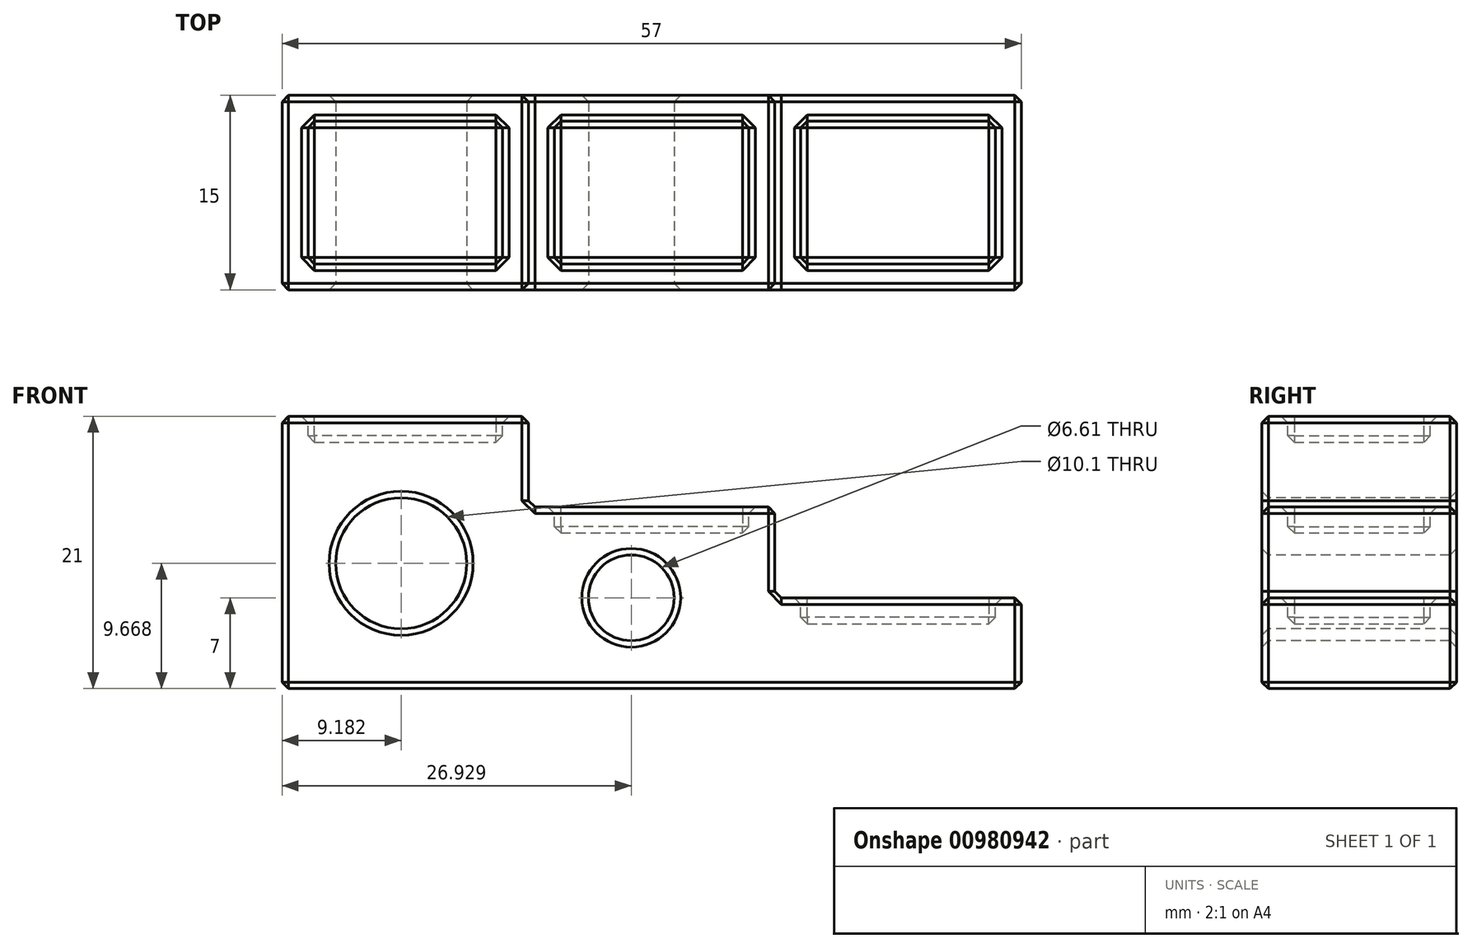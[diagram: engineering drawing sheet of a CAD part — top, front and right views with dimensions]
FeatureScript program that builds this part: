
annotation { "Feature Type Name" : "Feature", "Feature Type Description" : "" }
export const myFeature = defineFeature(function(context is Context, id is Id, definition is map)
    precondition{}
    {
        {
            var Q0;
            Q0=qCreatedBy(makeId("Front.planeOp"),FACE);
            var sketch = newSketch(context, id + "F0", { "sketchPlane" : qUnion([Q0])});
            skLineSegment(sketch, "E0", {"start": v(0, 0) * mm, "end": v(57, 0) * mm});
            skLineSegment(sketch, "E1", {"start": v(57, 0) * mm, "end": v(57, 7) * mm});
            skLineSegment(sketch, "E2", {"start": v(57, 7) * mm, "end": v(38, 7) * mm});
            skLineSegment(sketch, "E3", {"start": v(38, 7) * mm, "end": v(38, 14) * mm});
            skLineSegment(sketch, "E4", {"start": v(38, 14) * mm, "end": v(19, 14) * mm});
            skLineSegment(sketch, "E5", {"start": v(19, 14) * mm, "end": v(19, 21) * mm});
            skLineSegment(sketch, "E6", {"start": v(19, 21) * mm, "end": v(0, 21) * mm});
            skLineSegment(sketch, "E7", {"start": v(0, 21) * mm, "end": v(0, 0) * mm});
            skSolve(sketch);
        }
        {
            var Q0;
            Q0 = qSketchRegion(id + "F0", true);
            extrude(context, id + "F1", {"entities" : qUnion([Q0]), "depth" : 15 * mm, "offsetDistance" : 25 * mm});
        }
        {
            var Q0;
            Q0=makeQuery(id+"F1.opExtrude","SWEPT_FACE",FACE,{"disambiguationData":[OSD([sQuery(id+"F0.wireOp",EDGE,"E6")])]});
            var sketch = newSketch(context, id + "F2", { "sketchPlane" : qUnion([Q0])});
            skLineSegment(sketch, "E8.bottom", {"start": v(2, -13) * mm, "end": v(17, -13) * mm});
            skLineSegment(sketch, "E8.top", {"start": v(2, -2) * mm, "end": v(17, -2) * mm});
            skLineSegment(sketch, "E8.left", {"start": v(2, -13) * mm, "end": v(2, -2) * mm});
            skLineSegment(sketch, "E8.right", {"start": v(17, -13) * mm, "end": v(17, -2) * mm});
            skSolve(sketch);
        }
        {
            var Q0;
            Q0 = qSketchRegion(id + "F2", true);
            extrude(context, id + "F3", {"entities" : qUnion([Q0]), "operationType" : NewBodyOperationType.REMOVE, "oppositeDirection" : true, "depth" : 2 * mm, "offsetDistance" : 25 * mm});
        }
        {
            var Q0;
            Q0=makeQuery(id+"F1.opExtrude","SWEPT_FACE",FACE,{"disambiguationData":[OSD([sQuery(id+"F0.wireOp",EDGE,"E4")])]});
            var sketch = newSketch(context, id + "F4", { "sketchPlane" : qUnion([Q0])});
            skLineSegment(sketch, "E9.bottom", {"start": v(21, -13) * mm, "end": v(36, -13) * mm});
            skLineSegment(sketch, "E9.top", {"start": v(21, -2) * mm, "end": v(36, -2) * mm});
            skLineSegment(sketch, "E9.left", {"start": v(21, -13) * mm, "end": v(21, -2) * mm});
            skLineSegment(sketch, "E9.right", {"start": v(36, -13) * mm, "end": v(36, -2) * mm});
            skSolve(sketch);
        }
        {
            var Q0;
            Q0 = qSketchRegion(id + "F4", true);
            extrude(context, id + "F5", {"entities" : qUnion([Q0]), "operationType" : NewBodyOperationType.REMOVE, "oppositeDirection" : true, "depth" : 2 * mm, "offsetDistance" : 25 * mm});
        }
        {
            var Q0;
            Q0=makeQuery(id+"F1.opExtrude","SWEPT_FACE",FACE,{"disambiguationData":[OSD([sQuery(id+"F0.wireOp",EDGE,"E2")])]});
            var sketch = newSketch(context, id + "F6", { "sketchPlane" : qUnion([Q0])});
            skLineSegment(sketch, "E10.bottom", {"start": v(40, -13) * mm, "end": v(55, -13) * mm});
            skLineSegment(sketch, "E10.top", {"start": v(40, -2) * mm, "end": v(55, -2) * mm});
            skLineSegment(sketch, "E10.left", {"start": v(40, -13) * mm, "end": v(40, -2) * mm});
            skLineSegment(sketch, "E10.right", {"start": v(55, -13) * mm, "end": v(55, -2) * mm});
            skSolve(sketch);
        }
        {
            var Q0;
            Q0 = qSketchRegion(id + "F6", true);
            extrude(context, id + "F7", {"entities" : qUnion([Q0]), "operationType" : NewBodyOperationType.REMOVE, "oppositeDirection" : true, "depth" : 2 * mm, "offsetDistance" : 25 * mm});
        }
        {
            var Q0;
            Q0=makeQuery(id+"F1.opExtrude","CAP_FACE",FACE,{"disambiguationData":[OSD([sQuery(id+"F0.wireOp",EDGE,"E0"),sQuery(id+"F0.wireOp",EDGE,"E1"),sQuery(id+"F0.wireOp",EDGE,"E2"),sQuery(id+"F0.wireOp",EDGE,"E3"),sQuery(id+"F0.wireOp",EDGE,"E4"),sQuery(id+"F0.wireOp",EDGE,"E5"),sQuery(id+"F0.wireOp",EDGE,"E6"),sQuery(id+"F0.wireOp",EDGE,"E7")])],"isStart":false});
            var sketch = newSketch(context, id + "F8", { "sketchPlane" : qUnion([Q0])});
            skCircle(sketch, "E11", {"center": v(9.18, 9.67) * mm, "radius": 5.05 * mm});
            skCircle(sketch, "E12", {"center": v(26.93, 7) * mm, "radius": 3.3 * mm});
            skSolve(sketch);
        }
        {
            var Q0;
            Q0 = qSketchRegion(id + "F8", true);
            extrude(context, id + "F9", {"entities" : qUnion([Q0]), "operationType" : NewBodyOperationType.REMOVE, "oppositeDirection" : true, "depth" : 25 * mm, "offsetDistance" : 25 * mm});
        }
        {
            var Q0;
            Q0=makeQuery(id+"F1.opExtrude","CAP_EDGE",EDGE,{"disambiguationData":[OSD([sQuery(id+"F0.wireOp",EDGE,"E4")])],"isStart":true});
            var Q1;
            Q1=makeQuery(id+"F1.opExtrude","CAP_EDGE",EDGE,{"disambiguationData":[OSD([sQuery(id+"F0.wireOp",EDGE,"E4")])],"isStart":false});
            var Q2;
            Q2=makeQuery(id+"F1.opExtrude","CAP_EDGE",EDGE,{"disambiguationData":[OSD([sQuery(id+"F0.wireOp",EDGE,"E2")])],"isStart":true});
            var Q3;
            Q3=makeQuery(id+"F1.opExtrude","SWEPT_FACE",FACE,{"disambiguationData":[OSD([sQuery(id+"F0.wireOp",EDGE,"E7")])]});
            var Q4;
            Q4=makeQuery(id+"F1.opExtrude","CAP_EDGE",EDGE,{"disambiguationData":[OSD([sQuery(id+"F0.wireOp",EDGE,"E0")])],"isStart":false});
            var Q5;
            Q5=makeQuery(id+"F1.opExtrude","SWEPT_FACE",FACE,{"disambiguationData":[OSD([sQuery(id+"F0.wireOp",EDGE,"E5")])]});
            var Q6;
            Q6=makeQuery(id+"F1.opExtrude","SWEPT_EDGE",EDGE,{"disambiguationData":[OSD([sQuery(id+"F0.wireOp",EDGE,"E6"),sQuery(id+"F0.wireOp",EDGE,"E7")])]});
            var Q7;
            Q7=makeQuery(id+"F1.opExtrude","SWEPT_EDGE",EDGE,{"disambiguationData":[OSD([sQuery(id+"F0.wireOp",EDGE,"E5"),sQuery(id+"F0.wireOp",EDGE,"E6")])]});
            var Q8;
            Q8=makeQuery(id+"F1.opExtrude","SWEPT_FACE",FACE,{"disambiguationData":[OSD([sQuery(id+"F0.wireOp",EDGE,"E3")])]});
            var Q9;
            Q9=makeQuery(id+"F1.opExtrude","SWEPT_EDGE",EDGE,{"disambiguationData":[OSD([sQuery(id+"F0.wireOp",EDGE,"E4"),sQuery(id+"F0.wireOp",EDGE,"E5")])]});
            var Q10;
            Q10=makeQuery(id+"F1.opExtrude","SWEPT_EDGE",EDGE,{"disambiguationData":[OSD([sQuery(id+"F0.wireOp",EDGE,"E3"),sQuery(id+"F0.wireOp",EDGE,"E4")])]});
            var Q11;
            Q11=makeQuery(id+"F1.opExtrude","SWEPT_FACE",FACE,{"disambiguationData":[OSD([sQuery(id+"F0.wireOp",EDGE,"E1")])]});
            var Q12;
            Q12=makeQuery(id+"F1.opExtrude","SWEPT_EDGE",EDGE,{"disambiguationData":[OSD([sQuery(id+"F0.wireOp",EDGE,"E2"),sQuery(id+"F0.wireOp",EDGE,"E3")])]});
            var Q13;
            Q13=makeQuery(id+"F9.boolean.opBoolean","COPY",FACE,{"derivedFrom":makeQuery(id+"F9.opExtrude","SWEPT_FACE",FACE,{"disambiguationData":[OSD([sQuery(id+"F8.wireOp",EDGE,"E11")])]})});
            var Q14;
            Q14=makeQuery(id+"F1.opExtrude","SWEPT_EDGE",EDGE,{"disambiguationData":[OSD([sQuery(id+"F0.wireOp",EDGE,"E1"),sQuery(id+"F0.wireOp",EDGE,"E2")])]});
            var Q15;
            Q15=makeQuery(id+"F1.opExtrude","SWEPT_EDGE",EDGE,{"disambiguationData":[OSD([sQuery(id+"F0.wireOp",EDGE,"E0"),sQuery(id+"F0.wireOp",EDGE,"E1")])]});
            var Q16;
            Q16=makeQuery(id+"F1.opExtrude","SWEPT_FACE",FACE,{"disambiguationData":[OSD([sQuery(id+"F0.wireOp",EDGE,"E0")])]});
            var Q17;
            Q17=makeQuery(id+"F1.opExtrude","CAP_EDGE",EDGE,{"disambiguationData":[OSD([sQuery(id+"F0.wireOp",EDGE,"E2")])],"isStart":false});
            var Q18;
            Q18=makeQuery(id+"F1.opExtrude","CAP_EDGE",EDGE,{"disambiguationData":[OSD([sQuery(id+"F0.wireOp",EDGE,"E6")])],"isStart":true});
            var Q19;
            Q19=makeQuery(id+"F1.opExtrude","CAP_EDGE",EDGE,{"disambiguationData":[OSD([sQuery(id+"F0.wireOp",EDGE,"E6")])],"isStart":false});
            var Q20;
            Q20=makeQuery(id+"F3.boolean.opBoolean","COPY",FACE,{"derivedFrom":makeQuery(id+"F3.opExtrude","SWEPT_FACE",FACE,{"disambiguationData":[OSD([sQuery(id+"F2.wireOp",EDGE,"E8.bottom")])]})});
            var Q21;
            Q21=makeQuery(id+"F3.boolean.opBoolean","COPY",FACE,{"derivedFrom":makeQuery(id+"F3.opExtrude","CAP_FACE",FACE,{"disambiguationData":[OSD([sQuery(id+"F2.wireOp",EDGE,"E8.bottom"),sQuery(id+"F2.wireOp",EDGE,"E8.top"),sQuery(id+"F2.wireOp",EDGE,"E8.left"),sQuery(id+"F2.wireOp",EDGE,"E8.right")])],"isStart":false})});
            var Q22;
            Q22=makeQuery(id+"F3.boolean.opBoolean","COPY",FACE,{"derivedFrom":makeQuery(id+"F3.opExtrude","SWEPT_FACE",FACE,{"disambiguationData":[OSD([sQuery(id+"F2.wireOp",EDGE,"E8.top")])]})});
            var Q23;
            Q23=makeQuery(id+"F3.boolean.opBoolean","COPY",FACE,{"derivedFrom":makeQuery(id+"F3.opExtrude","SWEPT_FACE",FACE,{"disambiguationData":[OSD([sQuery(id+"F2.wireOp",EDGE,"E8.left")])]})});
            var Q24;
            Q24=makeQuery(id+"F3.boolean.opBoolean","COPY",EDGE,{"derivedFrom":makeQuery(id+"F3.opExtrude","CAP_EDGE",EDGE,{"disambiguationData":[OSD([sQuery(id+"F2.wireOp",EDGE,"E8.bottom")])],"isStart":true})});
            var Q25;
            Q25=makeQuery(id+"F3.boolean.opBoolean","COPY",FACE,{"derivedFrom":makeQuery(id+"F3.opExtrude","SWEPT_FACE",FACE,{"disambiguationData":[OSD([sQuery(id+"F2.wireOp",EDGE,"E8.right")])]})});
            var Q26;
            Q26=makeQuery(id+"F1.opExtrude","SWEPT_FACE",FACE,{"disambiguationData":[OSD([sQuery(id+"F0.wireOp",EDGE,"E6")])]});
            var Q27;
            Q27=makeQuery(id+"F3.boolean.opBoolean","COPY",EDGE,{"derivedFrom":makeQuery(id+"F3.opExtrude","CAP_EDGE",EDGE,{"disambiguationData":[OSD([sQuery(id+"F2.wireOp",EDGE,"E8.top")])],"isStart":true})});
            var Q28;
            Q28=makeQuery(id+"F3.boolean.opBoolean","COPY",EDGE,{"derivedFrom":makeQuery(id+"F3.opExtrude","CAP_EDGE",EDGE,{"disambiguationData":[OSD([sQuery(id+"F2.wireOp",EDGE,"E8.top")])],"isStart":false})});
            var Q29;
            Q29=makeQuery(id+"F3.boolean.opBoolean","COPY",EDGE,{"derivedFrom":makeQuery(id+"F3.opExtrude","CAP_EDGE",EDGE,{"disambiguationData":[OSD([sQuery(id+"F2.wireOp",EDGE,"E8.left")])],"isStart":false})});
            var Q30;
            Q30=makeQuery(id+"F5.boolean.opBoolean","COPY",FACE,{"derivedFrom":makeQuery(id+"F5.opExtrude","SWEPT_FACE",FACE,{"disambiguationData":[OSD([sQuery(id+"F4.wireOp",EDGE,"E9.bottom")])]})});
            var Q31;
            Q31=makeQuery(id+"F5.boolean.opBoolean","COPY",FACE,{"derivedFrom":makeQuery(id+"F5.opExtrude","CAP_FACE",FACE,{"disambiguationData":[OSD([sQuery(id+"F4.wireOp",EDGE,"E9.bottom"),sQuery(id+"F4.wireOp",EDGE,"E9.top"),sQuery(id+"F4.wireOp",EDGE,"E9.left"),sQuery(id+"F4.wireOp",EDGE,"E9.right")])],"isStart":false})});
            var Q32;
            Q32=makeQuery(id+"F5.boolean.opBoolean","COPY",FACE,{"derivedFrom":makeQuery(id+"F5.opExtrude","SWEPT_FACE",FACE,{"disambiguationData":[OSD([sQuery(id+"F4.wireOp",EDGE,"E9.top")])]})});
            var Q33;
            Q33=makeQuery(id+"F5.boolean.opBoolean","COPY",FACE,{"derivedFrom":makeQuery(id+"F5.opExtrude","SWEPT_FACE",FACE,{"disambiguationData":[OSD([sQuery(id+"F4.wireOp",EDGE,"E9.left")])]})});
            var Q34;
            Q34=makeQuery(id+"F5.boolean.opBoolean","COPY",EDGE,{"derivedFrom":makeQuery(id+"F5.opExtrude","CAP_EDGE",EDGE,{"disambiguationData":[OSD([sQuery(id+"F4.wireOp",EDGE,"E9.bottom")])],"isStart":true})});
            var Q35;
            Q35=makeQuery(id+"F5.boolean.opBoolean","COPY",FACE,{"derivedFrom":makeQuery(id+"F5.opExtrude","SWEPT_FACE",FACE,{"disambiguationData":[OSD([sQuery(id+"F4.wireOp",EDGE,"E9.right")])]})});
            var Q36;
            Q36=makeQuery(id+"F1.opExtrude","SWEPT_FACE",FACE,{"disambiguationData":[OSD([sQuery(id+"F0.wireOp",EDGE,"E4")])]});
            var Q37;
            Q37=makeQuery(id+"F5.boolean.opBoolean","COPY",EDGE,{"derivedFrom":makeQuery(id+"F5.opExtrude","CAP_EDGE",EDGE,{"disambiguationData":[OSD([sQuery(id+"F4.wireOp",EDGE,"E9.top")])],"isStart":false})});
            var Q38;
            Q38=makeQuery(id+"F7.boolean.opBoolean","COPY",FACE,{"derivedFrom":makeQuery(id+"F7.opExtrude","SWEPT_FACE",FACE,{"disambiguationData":[OSD([sQuery(id+"F6.wireOp",EDGE,"E10.bottom")])]})});
            var Q39;
            Q39=makeQuery(id+"F7.boolean.opBoolean","COPY",FACE,{"derivedFrom":makeQuery(id+"F7.opExtrude","CAP_FACE",FACE,{"disambiguationData":[OSD([sQuery(id+"F6.wireOp",EDGE,"E10.bottom"),sQuery(id+"F6.wireOp",EDGE,"E10.top"),sQuery(id+"F6.wireOp",EDGE,"E10.left"),sQuery(id+"F6.wireOp",EDGE,"E10.right")])],"isStart":false})});
            var Q40;
            Q40=makeQuery(id+"F7.boolean.opBoolean","COPY",FACE,{"derivedFrom":makeQuery(id+"F7.opExtrude","SWEPT_FACE",FACE,{"disambiguationData":[OSD([sQuery(id+"F6.wireOp",EDGE,"E10.top")])]})});
            var Q41;
            Q41=makeQuery(id+"F7.boolean.opBoolean","COPY",FACE,{"derivedFrom":makeQuery(id+"F7.opExtrude","SWEPT_FACE",FACE,{"disambiguationData":[OSD([sQuery(id+"F6.wireOp",EDGE,"E10.left")])]})});
            var Q42;
            Q42=makeQuery(id+"F7.boolean.opBoolean","COPY",FACE,{"derivedFrom":makeQuery(id+"F7.opExtrude","SWEPT_FACE",FACE,{"disambiguationData":[OSD([sQuery(id+"F6.wireOp",EDGE,"E10.right")])]})});
            var Q43;
            Q43=makeQuery(id+"F1.opExtrude","SWEPT_FACE",FACE,{"disambiguationData":[OSD([sQuery(id+"F0.wireOp",EDGE,"E2")])]});
            var Q44;
            Q44=makeQuery(id+"F7.boolean.opBoolean","COPY",EDGE,{"derivedFrom":makeQuery(id+"F7.opExtrude","CAP_EDGE",EDGE,{"disambiguationData":[OSD([sQuery(id+"F6.wireOp",EDGE,"E10.top")])],"isStart":true})});
            var Q45;
            Q45=makeQuery(id+"F7.boolean.opBoolean","COPY",EDGE,{"derivedFrom":makeQuery(id+"F7.opExtrude","CAP_EDGE",EDGE,{"disambiguationData":[OSD([sQuery(id+"F6.wireOp",EDGE,"E10.top")])],"isStart":false})});
            var Q46;
            Q46=makeQuery(id+"F1.opExtrude","CAP_FACE",FACE,{"disambiguationData":[OSD([sQuery(id+"F0.wireOp",EDGE,"E0"),sQuery(id+"F0.wireOp",EDGE,"E1"),sQuery(id+"F0.wireOp",EDGE,"E2"),sQuery(id+"F0.wireOp",EDGE,"E3"),sQuery(id+"F0.wireOp",EDGE,"E4"),sQuery(id+"F0.wireOp",EDGE,"E5"),sQuery(id+"F0.wireOp",EDGE,"E6"),sQuery(id+"F0.wireOp",EDGE,"E7")])],"isStart":false});
            var Q47;
            Q47=makeQuery(id+"F9.boolean.opBoolean","COPY",EDGE,{"derivedFrom":makeQuery(id+"F9.opExtrude","CAP_EDGE",EDGE,{"disambiguationData":[OSD([sQuery(id+"F8.wireOp",EDGE,"E12")])],"isStart":true})});
            var Q48;
            Q48=makeQuery(id+"F9.boolean.opBoolean","COPY",EDGE,{"derivedFrom":makeQuery(id+"F9.opExtrude","CAP_EDGE",EDGE,{"disambiguationData":[OSD([sQuery(id+"F8.wireOp",EDGE,"E11")])],"isStart":true})});
            var Q49;
            Q49=makeQuery(id+"F9.boolean.opBoolean","COPY",FACE,{"derivedFrom":makeQuery(id+"F9.opExtrude","SWEPT_FACE",FACE,{"disambiguationData":[OSD([sQuery(id+"F8.wireOp",EDGE,"E12")])]})});
            var Q50;
            Q50=makeQuery(id+"F1.opExtrude","CAP_EDGE",EDGE,{"disambiguationData":[OSD([sQuery(id+"F0.wireOp",EDGE,"E7")])],"isStart":false});
            var Q51;
            Q51=makeQuery(id+"F1.opExtrude","CAP_EDGE",EDGE,{"disambiguationData":[OSD([sQuery(id+"F0.wireOp",EDGE,"E1")])],"isStart":false});
            var Q52;
            Q52=makeQuery(id+"F1.opExtrude","CAP_EDGE",EDGE,{"disambiguationData":[OSD([sQuery(id+"F0.wireOp",EDGE,"E1")])],"isStart":true});
            var Q53;
            Q53=makeQuery(id+"F1.opExtrude","CAP_EDGE",EDGE,{"disambiguationData":[OSD([sQuery(id+"F0.wireOp",EDGE,"E0")])],"isStart":true});
            var Q54;
            Q54=makeQuery(id+"F1.opExtrude","SWEPT_EDGE",EDGE,{"disambiguationData":[OSD([sQuery(id+"F0.wireOp",EDGE,"E0"),sQuery(id+"F0.wireOp",EDGE,"E7")])]});
            var Q55;
            Q55=makeQuery(id+"F1.opExtrude","CAP_EDGE",EDGE,{"disambiguationData":[OSD([sQuery(id+"F0.wireOp",EDGE,"E3")])],"isStart":true});
            var Q56;
            Q56=makeQuery(id+"F1.opExtrude","CAP_EDGE",EDGE,{"disambiguationData":[OSD([sQuery(id+"F0.wireOp",EDGE,"E5")])],"isStart":true});
            var Q57;
            Q57=makeQuery(id+"F1.opExtrude","CAP_EDGE",EDGE,{"disambiguationData":[OSD([sQuery(id+"F0.wireOp",EDGE,"E5")])],"isStart":false});
            var Q58;
            Q58=makeQuery(id+"F1.opExtrude","CAP_EDGE",EDGE,{"disambiguationData":[OSD([sQuery(id+"F0.wireOp",EDGE,"E3")])],"isStart":false});
            var Q59;
            Q59=makeQuery(id+"F1.opExtrude","CAP_EDGE",EDGE,{"disambiguationData":[OSD([sQuery(id+"F0.wireOp",EDGE,"E7")])],"isStart":true});
            var Q60;
            Q60=makeQuery(id+"F3.boolean.opBoolean","COPY",EDGE,{"derivedFrom":makeQuery(id+"F3.opExtrude","SWEPT_EDGE",EDGE,{"disambiguationData":[OSD([sQuery(id+"F2.wireOp",EDGE,"E8.bottom"),sQuery(id+"F2.wireOp",EDGE,"E8.left")])]})});
            var Q61;
            Q61=makeQuery(id+"F3.boolean.opBoolean","COPY",EDGE,{"derivedFrom":makeQuery(id+"F3.opExtrude","SWEPT_EDGE",EDGE,{"disambiguationData":[OSD([sQuery(id+"F2.wireOp",EDGE,"E8.bottom"),sQuery(id+"F2.wireOp",EDGE,"E8.right")])]})});
            var Q62;
            Q62=makeQuery(id+"F3.boolean.opBoolean","COPY",EDGE,{"derivedFrom":makeQuery(id+"F3.opExtrude","SWEPT_EDGE",EDGE,{"disambiguationData":[OSD([sQuery(id+"F2.wireOp",EDGE,"E8.top"),sQuery(id+"F2.wireOp",EDGE,"E8.left")])]})});
            var Q63;
            Q63=makeQuery(id+"F3.boolean.opBoolean","COPY",EDGE,{"derivedFrom":makeQuery(id+"F3.opExtrude","SWEPT_EDGE",EDGE,{"disambiguationData":[OSD([sQuery(id+"F2.wireOp",EDGE,"E8.top"),sQuery(id+"F2.wireOp",EDGE,"E8.right")])]})});
            var Q64;
            Q64=makeQuery(id+"F3.boolean.opBoolean","COPY",EDGE,{"derivedFrom":makeQuery(id+"F3.opExtrude","CAP_EDGE",EDGE,{"disambiguationData":[OSD([sQuery(id+"F2.wireOp",EDGE,"E8.bottom")])],"isStart":false})});
            var Q65;
            Q65=makeQuery(id+"F3.boolean.opBoolean","COPY",EDGE,{"derivedFrom":makeQuery(id+"F3.opExtrude","CAP_EDGE",EDGE,{"disambiguationData":[OSD([sQuery(id+"F2.wireOp",EDGE,"E8.left")])],"isStart":true})});
            var Q66;
            Q66=makeQuery(id+"F3.boolean.opBoolean","COPY",EDGE,{"derivedFrom":makeQuery(id+"F3.opExtrude","CAP_EDGE",EDGE,{"disambiguationData":[OSD([sQuery(id+"F2.wireOp",EDGE,"E8.right")])],"isStart":true})});
            var Q67;
            Q67=makeQuery(id+"F3.boolean.opBoolean","COPY",EDGE,{"derivedFrom":makeQuery(id+"F3.opExtrude","CAP_EDGE",EDGE,{"disambiguationData":[OSD([sQuery(id+"F2.wireOp",EDGE,"E8.right")])],"isStart":false})});
            var Q68;
            Q68=makeQuery(id+"F5.boolean.opBoolean","COPY",EDGE,{"derivedFrom":makeQuery(id+"F5.opExtrude","SWEPT_EDGE",EDGE,{"disambiguationData":[OSD([sQuery(id+"F4.wireOp",EDGE,"E9.bottom"),sQuery(id+"F4.wireOp",EDGE,"E9.left")])]})});
            var Q69;
            Q69=makeQuery(id+"F5.boolean.opBoolean","COPY",EDGE,{"derivedFrom":makeQuery(id+"F5.opExtrude","SWEPT_EDGE",EDGE,{"disambiguationData":[OSD([sQuery(id+"F4.wireOp",EDGE,"E9.top"),sQuery(id+"F4.wireOp",EDGE,"E9.left")])]})});
            var Q70;
            Q70=makeQuery(id+"F5.boolean.opBoolean","COPY",EDGE,{"derivedFrom":makeQuery(id+"F5.opExtrude","SWEPT_EDGE",EDGE,{"disambiguationData":[OSD([sQuery(id+"F4.wireOp",EDGE,"E9.top"),sQuery(id+"F4.wireOp",EDGE,"E9.right")])]})});
            var Q71;
            Q71=makeQuery(id+"F5.boolean.opBoolean","COPY",EDGE,{"derivedFrom":makeQuery(id+"F5.opExtrude","CAP_EDGE",EDGE,{"disambiguationData":[OSD([sQuery(id+"F4.wireOp",EDGE,"E9.bottom")])],"isStart":false})});
            var Q72;
            Q72=makeQuery(id+"F5.boolean.opBoolean","COPY",EDGE,{"derivedFrom":makeQuery(id+"F5.opExtrude","CAP_EDGE",EDGE,{"disambiguationData":[OSD([sQuery(id+"F4.wireOp",EDGE,"E9.top")])],"isStart":true})});
            var Q73;
            Q73=makeQuery(id+"F5.boolean.opBoolean","COPY",EDGE,{"derivedFrom":makeQuery(id+"F5.opExtrude","CAP_EDGE",EDGE,{"disambiguationData":[OSD([sQuery(id+"F4.wireOp",EDGE,"E9.left")])],"isStart":true})});
            var Q74;
            Q74=makeQuery(id+"F5.boolean.opBoolean","COPY",EDGE,{"derivedFrom":makeQuery(id+"F5.opExtrude","CAP_EDGE",EDGE,{"disambiguationData":[OSD([sQuery(id+"F4.wireOp",EDGE,"E9.left")])],"isStart":false})});
            var Q75;
            Q75=makeQuery(id+"F5.boolean.opBoolean","COPY",EDGE,{"derivedFrom":makeQuery(id+"F5.opExtrude","CAP_EDGE",EDGE,{"disambiguationData":[OSD([sQuery(id+"F4.wireOp",EDGE,"E9.right")])],"isStart":true})});
            var Q76;
            Q76=makeQuery(id+"F5.boolean.opBoolean","COPY",EDGE,{"derivedFrom":makeQuery(id+"F5.opExtrude","CAP_EDGE",EDGE,{"disambiguationData":[OSD([sQuery(id+"F4.wireOp",EDGE,"E9.right")])],"isStart":false})});
            var Q77;
            Q77=makeQuery(id+"F7.boolean.opBoolean","COPY",EDGE,{"derivedFrom":makeQuery(id+"F7.opExtrude","SWEPT_EDGE",EDGE,{"disambiguationData":[OSD([sQuery(id+"F6.wireOp",EDGE,"E10.bottom"),sQuery(id+"F6.wireOp",EDGE,"E10.left")])]})});
            var Q78;
            Q78=makeQuery(id+"F7.boolean.opBoolean","COPY",EDGE,{"derivedFrom":makeQuery(id+"F7.opExtrude","SWEPT_EDGE",EDGE,{"disambiguationData":[OSD([sQuery(id+"F6.wireOp",EDGE,"E10.bottom"),sQuery(id+"F6.wireOp",EDGE,"E10.right")])]})});
            var Q79;
            Q79=makeQuery(id+"F7.boolean.opBoolean","COPY",EDGE,{"derivedFrom":makeQuery(id+"F7.opExtrude","SWEPT_EDGE",EDGE,{"disambiguationData":[OSD([sQuery(id+"F6.wireOp",EDGE,"E10.top"),sQuery(id+"F6.wireOp",EDGE,"E10.left")])]})});
            var Q80;
            Q80=makeQuery(id+"F7.boolean.opBoolean","COPY",EDGE,{"derivedFrom":makeQuery(id+"F7.opExtrude","SWEPT_EDGE",EDGE,{"disambiguationData":[OSD([sQuery(id+"F6.wireOp",EDGE,"E10.top"),sQuery(id+"F6.wireOp",EDGE,"E10.right")])]})});
            var Q81;
            Q81=makeQuery(id+"F7.boolean.opBoolean","COPY",EDGE,{"derivedFrom":makeQuery(id+"F7.opExtrude","CAP_EDGE",EDGE,{"disambiguationData":[OSD([sQuery(id+"F6.wireOp",EDGE,"E10.bottom")])],"isStart":true})});
            var Q82;
            Q82=makeQuery(id+"F7.boolean.opBoolean","COPY",EDGE,{"derivedFrom":makeQuery(id+"F7.opExtrude","CAP_EDGE",EDGE,{"disambiguationData":[OSD([sQuery(id+"F6.wireOp",EDGE,"E10.bottom")])],"isStart":false})});
            var Q83;
            Q83=makeQuery(id+"F7.boolean.opBoolean","COPY",EDGE,{"derivedFrom":makeQuery(id+"F7.opExtrude","CAP_EDGE",EDGE,{"disambiguationData":[OSD([sQuery(id+"F6.wireOp",EDGE,"E10.left")])],"isStart":true})});
            var Q84;
            Q84=makeQuery(id+"F7.boolean.opBoolean","COPY",EDGE,{"derivedFrom":makeQuery(id+"F7.opExtrude","CAP_EDGE",EDGE,{"disambiguationData":[OSD([sQuery(id+"F6.wireOp",EDGE,"E10.left")])],"isStart":false})});
            var Q85;
            Q85=makeQuery(id+"F7.boolean.opBoolean","COPY",EDGE,{"derivedFrom":makeQuery(id+"F7.opExtrude","CAP_EDGE",EDGE,{"disambiguationData":[OSD([sQuery(id+"F6.wireOp",EDGE,"E10.right")])],"isStart":true})});
            var Q86;
            Q86=makeQuery(id+"F7.boolean.opBoolean","COPY",EDGE,{"derivedFrom":makeQuery(id+"F7.opExtrude","CAP_EDGE",EDGE,{"disambiguationData":[OSD([sQuery(id+"F6.wireOp",EDGE,"E10.right")])],"isStart":false})});
            var Q87;
            Q87=makeQuery(id+"F9.boolean.opBoolean","INTERSECT",EDGE,{"derivedFrom":[makeQuery(id+"F1.opExtrude","CAP_FACE",FACE,{"disambiguationData":[OSD([sQuery(id+"F0.wireOp",EDGE,"E0"),sQuery(id+"F0.wireOp",EDGE,"E1"),sQuery(id+"F0.wireOp",EDGE,"E2"),sQuery(id+"F0.wireOp",EDGE,"E3"),sQuery(id+"F0.wireOp",EDGE,"E4"),sQuery(id+"F0.wireOp",EDGE,"E5"),sQuery(id+"F0.wireOp",EDGE,"E6"),sQuery(id+"F0.wireOp",EDGE,"E7")])],"isStart":true}),makeQuery(id+"F9.opExtrude","SWEPT_FACE",FACE,{"disambiguationData":[OSD([sQuery(id+"F8.wireOp",EDGE,"E12")])]})]});
            var Q88;
            Q88=makeQuery(id+"F1.opExtrude","CAP_FACE",FACE,{"disambiguationData":[OSD([sQuery(id+"F0.wireOp",EDGE,"E0"),sQuery(id+"F0.wireOp",EDGE,"E1"),sQuery(id+"F0.wireOp",EDGE,"E2"),sQuery(id+"F0.wireOp",EDGE,"E3"),sQuery(id+"F0.wireOp",EDGE,"E4"),sQuery(id+"F0.wireOp",EDGE,"E5"),sQuery(id+"F0.wireOp",EDGE,"E6"),sQuery(id+"F0.wireOp",EDGE,"E7")])],"isStart":true});
            var Q89;
            Q89=makeQuery(id+"F9.boolean.opBoolean","INTERSECT",EDGE,{"derivedFrom":[makeQuery(id+"F1.opExtrude","CAP_FACE",FACE,{"disambiguationData":[OSD([sQuery(id+"F0.wireOp",EDGE,"E0"),sQuery(id+"F0.wireOp",EDGE,"E1"),sQuery(id+"F0.wireOp",EDGE,"E2"),sQuery(id+"F0.wireOp",EDGE,"E3"),sQuery(id+"F0.wireOp",EDGE,"E4"),sQuery(id+"F0.wireOp",EDGE,"E5"),sQuery(id+"F0.wireOp",EDGE,"E6"),sQuery(id+"F0.wireOp",EDGE,"E7")])],"isStart":true}),makeQuery(id+"F9.opExtrude","SWEPT_FACE",FACE,{"disambiguationData":[OSD([sQuery(id+"F8.wireOp",EDGE,"E11")])]})]});
            var Q90;
            Q90=makeQuery(id+"F5.boolean.opBoolean","COPY",EDGE,{"derivedFrom":makeQuery(id+"F5.opExtrude","SWEPT_EDGE",EDGE,{"disambiguationData":[OSD([sQuery(id+"F4.wireOp",EDGE,"E9.bottom"),sQuery(id+"F4.wireOp",EDGE,"E9.right")])]})});
            chamfer(context, id + "F10", {"entities" : qUnion([Q0, Q1, Q2, Q3, Q4, Q5, Q6, Q7, Q8, Q9, Q10, Q11, Q12, Q13, Q14, Q15, Q16, Q17, Q18, Q19, Q20, Q21, Q22, Q23, Q24, Q25, Q26, Q27, Q28, Q29, Q30, Q31, Q32, Q33, Q34, Q35, Q36, Q37, Q38, Q39, Q40, Q41, Q42, Q43, Q44, Q45, Q46, Q47, Q48, Q49, Q50, Q51, Q52, Q53, Q54, Q55, Q56, Q57, Q58, Q59, Q60, Q61, Q62, Q63, Q64, Q65, Q66, Q67, Q68, Q69, Q70, Q71, Q72, Q73, Q74, Q75, Q76, Q77, Q78, Q79, Q80, Q81, Q82, Q83, Q84, Q85, Q86, Q87, Q88, Q89, Q90]), "width" : 0.5 * mm, "tangentPropagation" : true});
        }
    });
